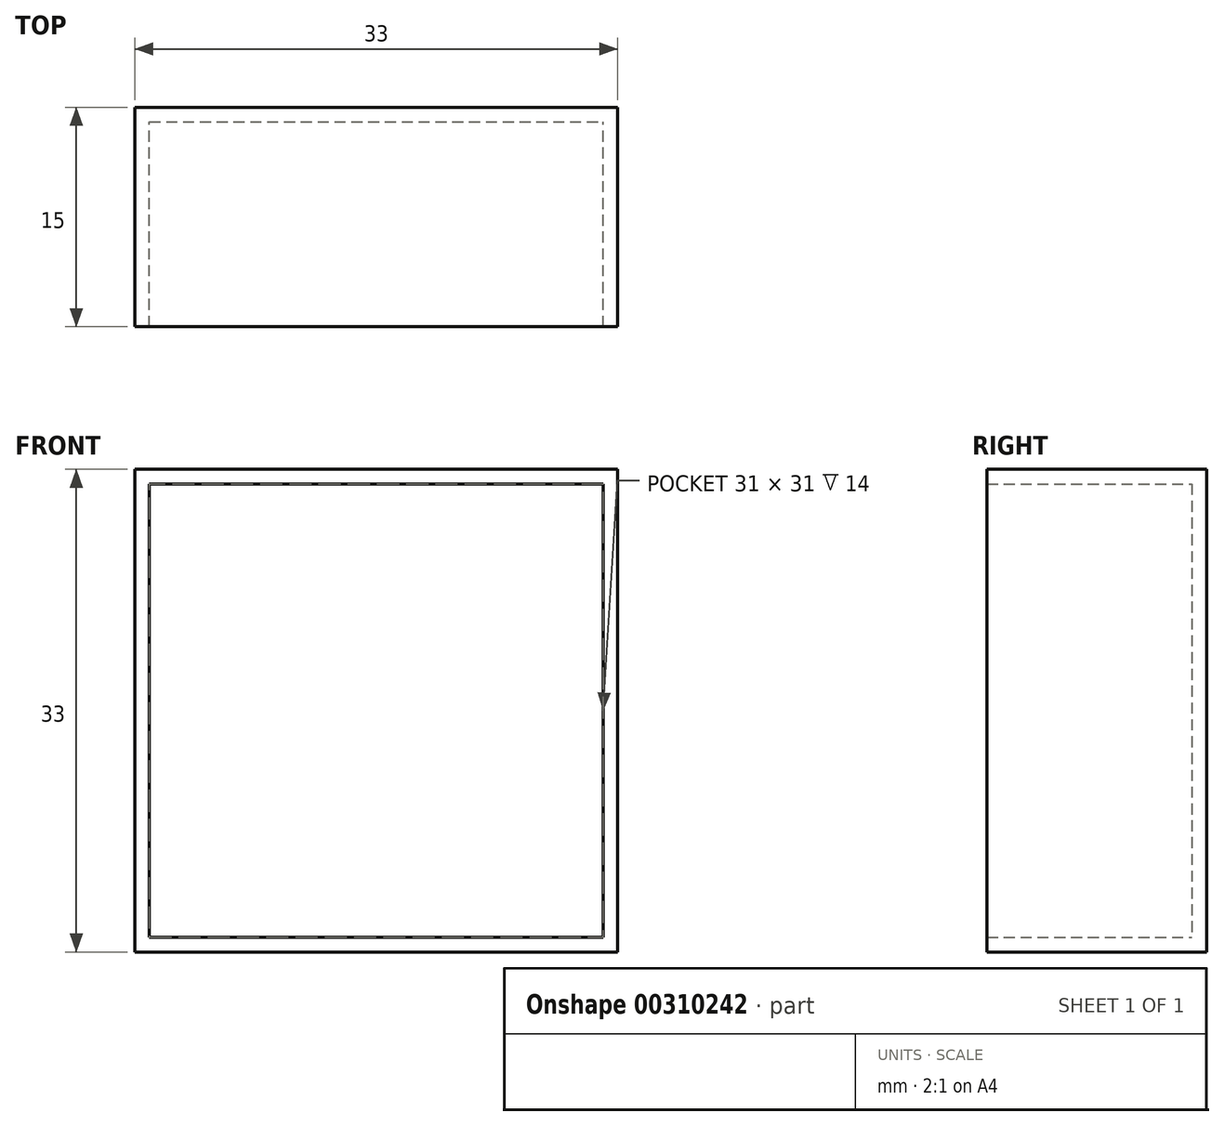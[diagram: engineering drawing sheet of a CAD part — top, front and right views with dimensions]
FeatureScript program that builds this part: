
annotation { "Feature Type Name" : "Feature", "Feature Type Description" : "" }
export const myFeature = defineFeature(function(context is Context, id is Id, definition is map)
    precondition{}
    {
        {
            var Q0;
            Q0=qCreatedBy(makeId("Front.planeOp"),FACE);
            var sketch = newSketch(context, id + "F0", { "sketchPlane" : qUnion([Q0])});
            skLineSegment(sketch, "E0.bottom", {"start": v(-16.5, 16.5) * mm, "end": v(16.5, 16.5) * mm});
            skLineSegment(sketch, "E0.top", {"start": v(-16.5, -16.5) * mm, "end": v(16.5, -16.5) * mm});
            skLineSegment(sketch, "E0.left", {"start": v(-16.5, 16.5) * mm, "end": v(-16.5, -16.5) * mm});
            skLineSegment(sketch, "E0.right", {"start": v(16.5, 16.5) * mm, "end": v(16.5, -16.5) * mm});
            skLineSegment(sketch, "E1", {"start": v(-16.5, 16.5) * mm, "end": v(16.5, -16.5) * mm, "construction": true});
            skSolve(sketch);
        }
        {
            var Q0;
            Q0 = qSketchRegion(id + "F0", true);
            extrude(context, id + "F1", {"entities" : qUnion([Q0]), "depth" : 15 * mm});
        }
        {
            var Q0;
            Q0=makeQuery(id+"F1.opExtrude","CAP_FACE",FACE,{"disambiguationData":[OSD([sQuery(id+"F0.wireOp",EDGE,"E0.bottom"),sQuery(id+"F0.wireOp",EDGE,"E0.top"),sQuery(id+"F0.wireOp",EDGE,"E0.left"),sQuery(id+"F0.wireOp",EDGE,"E0.right")])],"isStart":false});
            shell(context, id + "F2", {"entities" : qUnion([Q0]), "thickness" : 1 * mm});
        }
    });
